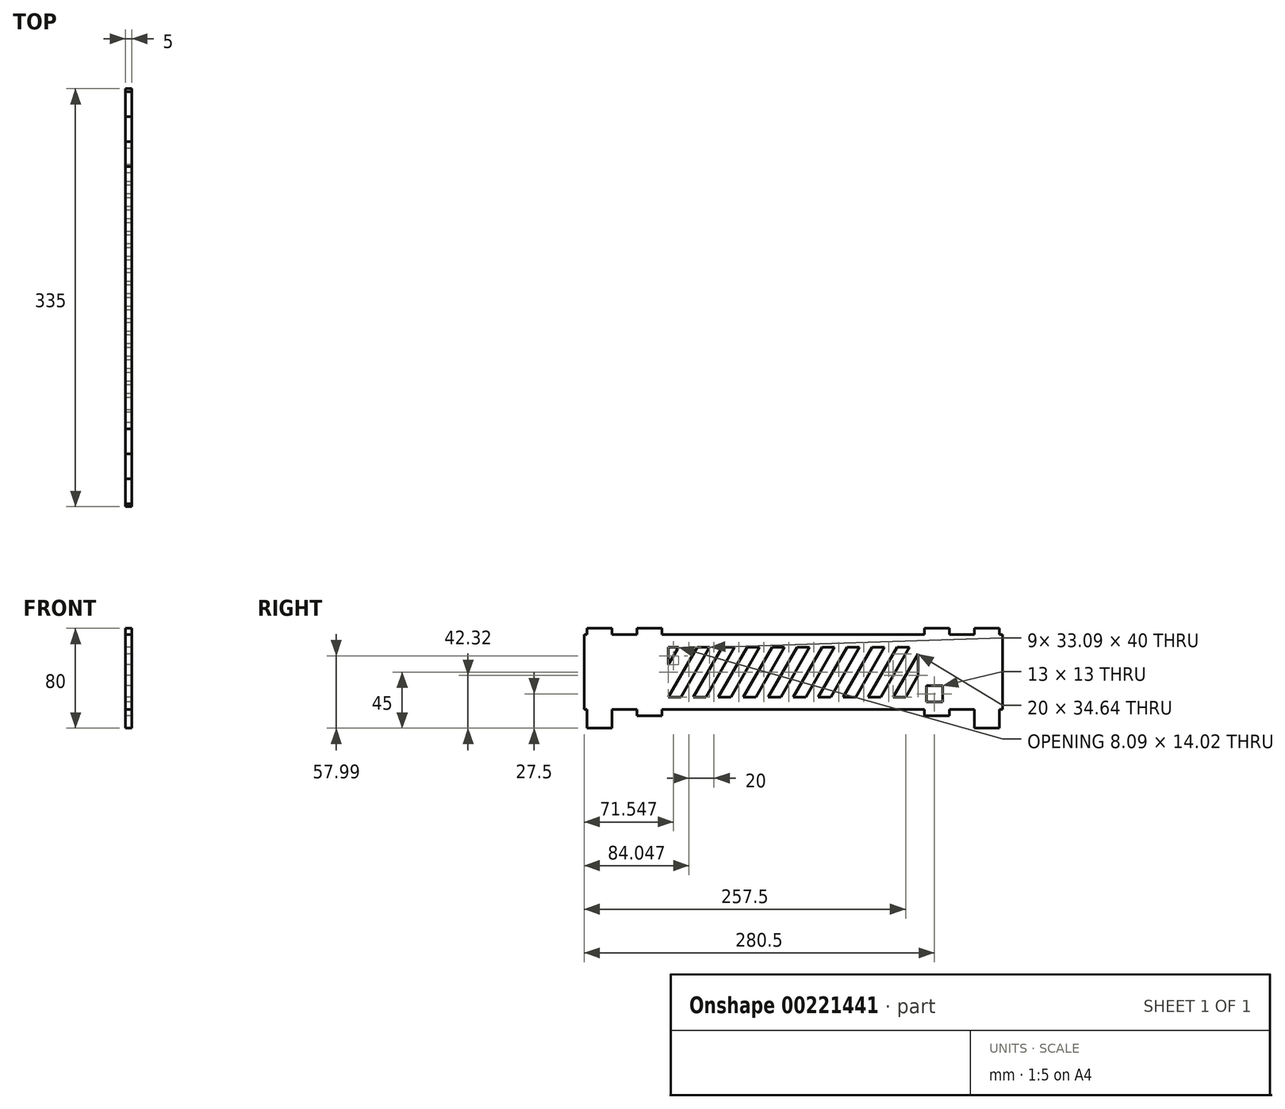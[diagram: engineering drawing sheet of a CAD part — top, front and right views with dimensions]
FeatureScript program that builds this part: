
annotation { "Feature Type Name" : "Feature", "Feature Type Description" : "" }
export const myFeature = defineFeature(function(context is Context, id is Id, definition is map)
    precondition{}
    {
        {
            assignVariable(context, id + "F0", {"name" : "thickness", "anyValue" : 5 * mm});
        }
        {
            var Q0;
            Q0=qCreatedBy(makeId("Right.planeOp"),FACE);
            var sketch = newSketch(context, id + "F1", { "sketchPlane" : qUnion([Q0])});
            skLineSegment(sketch, "E0.bottom", {"start": v(0, 0) * mm, "end": v(335, 0) * mm});
            skLineSegment(sketch, "E0.top", {"start": v(0, 60) * mm, "end": v(335, 60) * mm});
            skLineSegment(sketch, "E0.left", {"start": v(0, 0) * mm, "end": v(0, 60) * mm});
            skLineSegment(sketch, "E0.right", {"start": v(335, 0) * mm, "end": v(335, 60) * mm});
            skLineSegment(sketch, "E1", {"start": v(332.5, 0) * mm, "end": v(332.5, -15) * mm});
            skLineSegment(sketch, "E2", {"start": v(332.5, -15) * mm, "end": v(312.5, -15) * mm});
            skLineSegment(sketch, "E3", {"start": v(312.5, -15) * mm, "end": v(312.5, 0) * mm});
            skLineSegment(sketch, "E4", {"start": v(292.5, 0) * mm, "end": v(292.5, -5) * mm});
            skLineSegment(sketch, "E5", {"start": v(292.5, -5) * mm, "end": v(272.5, -5) * mm});
            skLineSegment(sketch, "E6", {"start": v(272.5, -5) * mm, "end": v(272.5, 0) * mm});
            skLineSegment(sketch, "E7", {"start": v(167.5, 60) * mm, "end": v(167.5, 0) * mm, "construction": true});
            skLineSegment(sketch, "E8", {"start": v(0, 30) * mm, "end": v(335, 30) * mm, "construction": true});
            skLineSegment(sketch, "E9.MirrorCS", {"start": v(62.5, -5) * mm, "end": v(62.5, 0) * mm});
            skLineSegment(sketch, "E10.MirrorCS", {"start": v(42.5, 0) * mm, "end": v(42.5, -5) * mm});
            skLineSegment(sketch, "E11.MirrorCS", {"start": v(42.5, -5) * mm, "end": v(62.5, -5) * mm});
            skLineSegment(sketch, "E12.MirrorCS", {"start": v(2.5, 0) * mm, "end": v(2.5, -15) * mm});
            skLineSegment(sketch, "E13.MirrorCS", {"start": v(2.5, -15) * mm, "end": v(22.5, -15) * mm});
            skLineSegment(sketch, "E14.MirrorCS", {"start": v(22.5, -15) * mm, "end": v(22.5, 0) * mm});
            skLineSegment(sketch, "E15.MirrorCS", {"start": v(62.5, 65) * mm, "end": v(62.5, 60) * mm});
            skLineSegment(sketch, "E16.MirrorCS", {"start": v(42.5, 60) * mm, "end": v(42.5, 65) * mm});
            skLineSegment(sketch, "E17.MirrorCS", {"start": v(42.5, 65) * mm, "end": v(62.5, 65) * mm});
            skLineSegment(sketch, "E18.MirrorCS", {"start": v(272.5, 65) * mm, "end": v(272.5, 60) * mm});
            skLineSegment(sketch, "E19.MirrorCS", {"start": v(292.5, 60) * mm, "end": v(292.5, 65) * mm});
            skLineSegment(sketch, "E20.MirrorCS", {"start": v(292.5, 65) * mm, "end": v(272.5, 65) * mm});
            skLineSegment(sketch, "E21", {"start": v(2.5, 60) * mm, "end": v(2.5, 65) * mm});
            skLineSegment(sketch, "E22", {"start": v(2.5, 65) * mm, "end": v(22.5, 65) * mm});
            skLineSegment(sketch, "E23", {"start": v(22.5, 65) * mm, "end": v(22.5, 60) * mm});
            skLineSegment(sketch, "E24.MirrorCS", {"start": v(332.5, 65) * mm, "end": v(312.5, 65) * mm});
            skLineSegment(sketch, "E25.MirrorCS", {"start": v(312.5, 65) * mm, "end": v(312.5, 60) * mm});
            skLineSegment(sketch, "E26.MirrorCS", {"start": v(332.5, 60) * mm, "end": v(332.5, 65) * mm});
            skLineSegment(sketch, "E27.bottom", {"start": v(274, 19) * mm, "end": v(287, 19) * mm});
            skLineSegment(sketch, "E27.top", {"start": v(274, 6) * mm, "end": v(287, 6) * mm});
            skLineSegment(sketch, "E27.left", {"start": v(274, 19) * mm, "end": v(274, 6) * mm});
            skLineSegment(sketch, "E27.right", {"start": v(287, 19) * mm, "end": v(287, 6) * mm});
            skLineSegment(sketch, "E28.bottom", {"start": v(67.5, 50) * mm, "end": v(267.5, 50) * mm, "construction": true});
            skLineSegment(sketch, "E28.top", {"start": v(67.5, 10) * mm, "end": v(267.5, 10) * mm, "construction": true});
            skLineSegment(sketch, "E28.left", {"start": v(67.5, 50) * mm, "end": v(67.5, 10) * mm, "construction": true});
            skLineSegment(sketch, "E28.right", {"start": v(267.5, 50) * mm, "end": v(267.5, 10) * mm, "construction": true});
            skPoint(sketch, "E29", {"position": v(167.5, 50) * mm});
            skPoint(sketch, "E30", {"position": v(67.5, 30) * mm});
            skLineSegment(sketch, "E31", {"start": v(67.5, 10) * mm, "end": v(90.6, 50) * mm});
            skLineSegment(sketch, "E32", {"start": v(90.6, 50) * mm, "end": v(100.6, 50) * mm});
            skLineSegment(sketch, "E33", {"start": v(100.6, 50) * mm, "end": v(77.5, 10) * mm});
            skLineSegment(sketch, "E34", {"start": v(77.5, 10) * mm, "end": v(67.5, 10) * mm});
            skLineSegment(sketch, "E35.1.0.0", {"start": v(87.5, 10) * mm, "end": v(110.6, 50) * mm});
            skLineSegment(sketch, "E35.1.0.1", {"start": v(120.6, 50) * mm, "end": v(97.5, 10) * mm});
            skLineSegment(sketch, "E35.1.0.2", {"start": v(110.6, 50) * mm, "end": v(120.6, 50) * mm});
            skLineSegment(sketch, "E35.1.0.3", {"start": v(97.5, 10) * mm, "end": v(87.5, 10) * mm});
            skLineSegment(sketch, "E35.2.0.0", {"start": v(107.5, 10) * mm, "end": v(130.6, 50) * mm});
            skLineSegment(sketch, "E35.2.0.1", {"start": v(140.6, 50) * mm, "end": v(117.5, 10) * mm});
            skLineSegment(sketch, "E35.2.0.2", {"start": v(130.6, 50) * mm, "end": v(140.6, 50) * mm});
            skLineSegment(sketch, "E35.2.0.3", {"start": v(117.5, 10) * mm, "end": v(107.5, 10) * mm});
            skLineSegment(sketch, "E35.3.0.0", {"start": v(127.5, 10) * mm, "end": v(150.6, 50) * mm});
            skLineSegment(sketch, "E35.3.0.1", {"start": v(160.6, 50) * mm, "end": v(137.5, 10) * mm});
            skLineSegment(sketch, "E35.3.0.2", {"start": v(150.6, 50) * mm, "end": v(160.6, 50) * mm});
            skLineSegment(sketch, "E35.3.0.3", {"start": v(137.5, 10) * mm, "end": v(127.5, 10) * mm});
            skLineSegment(sketch, "E35.4.0.0", {"start": v(147.5, 10) * mm, "end": v(170.6, 50) * mm});
            skLineSegment(sketch, "E35.4.0.1", {"start": v(180.6, 50) * mm, "end": v(157.5, 10) * mm});
            skLineSegment(sketch, "E35.4.0.2", {"start": v(170.6, 50) * mm, "end": v(180.6, 50) * mm});
            skLineSegment(sketch, "E35.4.0.3", {"start": v(157.5, 10) * mm, "end": v(147.5, 10) * mm});
            skLineSegment(sketch, "E35.5.0.0", {"start": v(167.5, 10) * mm, "end": v(190.6, 50) * mm});
            skLineSegment(sketch, "E35.5.0.1", {"start": v(200.6, 50) * mm, "end": v(177.5, 10) * mm});
            skLineSegment(sketch, "E35.5.0.2", {"start": v(190.6, 50) * mm, "end": v(200.6, 50) * mm});
            skLineSegment(sketch, "E35.5.0.3", {"start": v(177.5, 10) * mm, "end": v(167.5, 10) * mm});
            skLineSegment(sketch, "E35.6.0.0", {"start": v(187.5, 10) * mm, "end": v(210.6, 50) * mm});
            skLineSegment(sketch, "E35.6.0.1", {"start": v(220.6, 50) * mm, "end": v(197.5, 10) * mm});
            skLineSegment(sketch, "E35.6.0.2", {"start": v(210.6, 50) * mm, "end": v(220.6, 50) * mm});
            skLineSegment(sketch, "E35.6.0.3", {"start": v(197.5, 10) * mm, "end": v(187.5, 10) * mm});
            skLineSegment(sketch, "E35.7.0.0", {"start": v(207.5, 10) * mm, "end": v(230.6, 50) * mm});
            skLineSegment(sketch, "E35.7.0.1", {"start": v(240.6, 50) * mm, "end": v(217.5, 10) * mm});
            skLineSegment(sketch, "E35.7.0.2", {"start": v(230.6, 50) * mm, "end": v(240.6, 50) * mm});
            skLineSegment(sketch, "E35.7.0.3", {"start": v(217.5, 10) * mm, "end": v(207.5, 10) * mm});
            skLineSegment(sketch, "E35.8.0.0", {"start": v(227.5, 10) * mm, "end": v(250.6, 50) * mm});
            skLineSegment(sketch, "E35.8.0.1", {"start": v(260.6, 50) * mm, "end": v(237.5, 10) * mm});
            skLineSegment(sketch, "E35.8.0.2", {"start": v(250.6, 50) * mm, "end": v(260.6, 50) * mm});
            skLineSegment(sketch, "E35.8.0.3", {"start": v(237.5, 10) * mm, "end": v(227.5, 10) * mm});
            skLineSegment(sketch, "E35.9.0.0", {"start": v(247.5, 10) * mm, "end": v(267.5, 44.64) * mm});
            skLineSegment(sketch, "E35.9.0.1", {"start": v(267.5, 27.32) * mm, "end": v(257.5, 10) * mm});
            skLineSegment(sketch, "E35.9.0.3", {"start": v(257.5, 10) * mm, "end": v(247.5, 10) * mm});
            skLineSegment(sketch, "E35.direction1", {"start": v(67.5, 10) * mm, "end": v(87.5, 10) * mm, "construction": true});
            skLineSegment(sketch, "E36.1.0.1", {"start": v(67.5, 50) * mm, "end": v(75.6, 50) * mm});
            skLineSegment(sketch, "E36.1.0.2", {"start": v(75.6, 50) * mm, "end": v(67.5, 35.98) * mm});
            skLineSegment(sketch, "E36.direction1", {"start": v(67.5, 10) * mm, "end": v(42.5, 10) * mm, "construction": true});
            skLineSegment(sketch, "E37", {"start": v(67.5, 35.98) * mm, "end": v(67.5, 50) * mm});
            skLineSegment(sketch, "E38", {"start": v(267.5, 27.32) * mm, "end": v(267.5, 44.64) * mm});
            skSolve(sketch);
        }
        {
            var Q0;
            Q0=qSketchRegion(id+"F1",true);
            extrude(context, id + "F2", {"entities" : qUnion([Q0]), "depth" : getVariable(context, 'thickness')});
        }
    });
